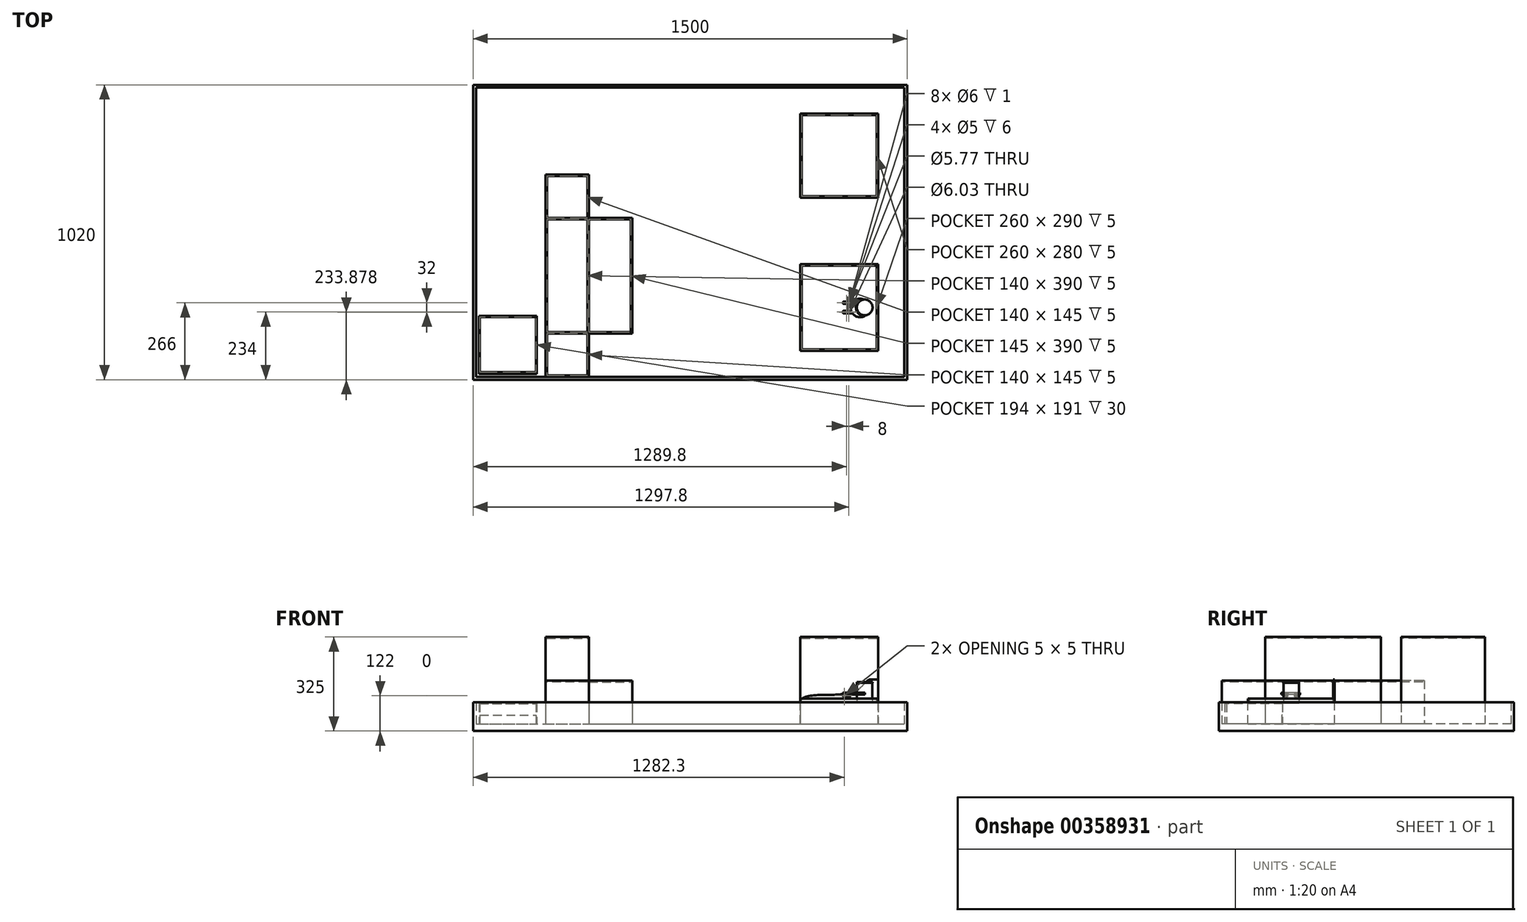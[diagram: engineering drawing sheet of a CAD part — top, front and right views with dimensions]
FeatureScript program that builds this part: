
annotation { "Feature Type Name" : "Feature", "Feature Type Description" : "" }
export const myFeature = defineFeature(function(context is Context, id is Id, definition is map)
    precondition{}
    {
        {
            var Q0;
            Q0=qCreatedBy(makeId("Top.planeOp"),FACE);
            var sketch = newSketch(context, id + "F0", { "sketchPlane" : qUnion([Q0])});
            skCircle(sketch, "E0", {"center": v(0, 0) * mm, "radius": 27.2 * mm});
            skSolve(sketch);
        }
        {
            var Q0;
            Q0=qSketchRegion(id+"F0",true);
            extrude(context, id + "F1", {"entities" : qUnion([Q0]), "depth" : 2.83 * mm});
        }
        {
            var Q0;
            Q0=makeQuery(id+"F1.opExtrude","CAP_FACE",FACE,{"disambiguationData":[OSD([sQuery(id+"F0.wireOp",EDGE,"E0")])],"isStart":false});
            var sketch = newSketch(context, id + "F2", { "sketchPlane" : qUnion([Q0])});
            skCircle(sketch, "E1", {"center": v(0, 0) * mm, "radius": 26.4 * mm});
            skSolve(sketch);
        }
        {
            var Q0;
            Q0=qSketchRegion(id+"F2",true);
            extrude(context, id + "F3", {"entities" : qUnion([Q0]), "operationType" : NewBodyOperationType.ADD, "depth" : 67.36 * mm});
        }
        {
            var Q0;
            Q0=makeQuery(id+"F3.opExtrude","CAP_FACE",FACE,{"disambiguationData":[OSD([sQuery(id+"F2.wireOp",EDGE,"E1")])],"isStart":false});
            var sketch = newSketch(context, id + "F4", { "sketchPlane" : qUnion([Q0])});
            skCircle(sketch, "E2", {"center": v(0, 0) * mm, "radius": 27.2 * mm});
            skSolve(sketch);
        }
        {
            var Q0;
            Q0=qSketchRegion(id+"F4",true);
            extrude(context, id + "F5", {"entities" : qUnion([Q0]), "operationType" : NewBodyOperationType.ADD, "depth" : 2.83 * mm});
        }
        {
            var Q0;
            Q0=makeQuery(id+"F5.opExtrude","CAP_FACE",FACE,{"disambiguationData":[OSD([sQuery(id+"F4.wireOp",EDGE,"E2")])],"isStart":false});
            var sketch = newSketch(context, id + "F6", { "sketchPlane" : qUnion([Q0])});
            skSolve(sketch);
        }
        {
            var Q0;
            Q0=qCreatedBy(makeId("Top.planeOp"),FACE);
            cPlane(context, id + "F7", {"entities" : qUnion([Q0]), "cplaneType" : CPlaneType.OFFSET, "offset" : 25 * mm, "width" : 150 * mm, "height" : 150 * mm});
        }
        {
            var Q0;
            Q0=makeQuery(id+"F6.imprint","IMPRINT",FACE,{"disambiguationData":[TD([[makeQuery(id+"F6.imprint","IMPRINT",EDGE,{"derivedFrom":makeQuery(id+"F5.opExtrude","CAP_EDGE",EDGE,{"disambiguationData":[OSD([sQuery(id+"F4.wireOp",EDGE,"E2")])],"isStart":false})}),1.0]])]});
            var sketch = newSketch(context, id + "F8", { "sketchPlane" : qUnion([Q0])});
            skSolve(sketch);
        }
        {
            var Q0;
            Q0=qCreatedBy(makeId("Top.planeOp"),FACE);
            var sketch = newSketch(context, id + "F9", { "sketchPlane" : qUnion([Q0])});
            skLineSegment(sketch, "E3.bottom", {"start": v(-222.8, -150) * mm, "end": v(47.2, -150) * mm});
            skLineSegment(sketch, "E3.top", {"start": v(-222.8, 150) * mm, "end": v(47.2, 150) * mm});
            skLineSegment(sketch, "E3.left", {"start": v(-222.8, -150) * mm, "end": v(-222.8, 150) * mm});
            skLineSegment(sketch, "E3.right", {"start": v(47.2, -150) * mm, "end": v(47.2, 150) * mm});
            skSolve(sketch);
        }
        {
            var Q0;
            Q0=qSketchRegion(id+"F9",true);
            extrude(context, id + "F10", {"entities" : qUnion([Q0]), "oppositeDirection" : true, "depth" : 72 * mm});
        }
        {
            var Q0;
            Q0=makeQuery(id+"F10.opExtrude","CAP_FACE",FACE,{"disambiguationData":[OSD([sQuery(id+"F9.wireOp",EDGE,"E3.bottom"),sQuery(id+"F9.wireOp",EDGE,"E3.top"),sQuery(id+"F9.wireOp",EDGE,"E3.left"),sQuery(id+"F9.wireOp",EDGE,"E3.right")])],"isStart":true});
            var sketch = newSketch(context, id + "F11", { "sketchPlane" : qUnion([Q0])});
            skLineSegment(sketch, "E4.bottom", {"start": v(-222.8, -150) * mm, "end": v(47.2, -150) * mm});
            skLineSegment(sketch, "E4.top", {"start": v(-222.8, -145) * mm, "end": v(42.2, -145) * mm});
            skLineSegment(sketch, "E4.left", {"start": v(-222.8, -150) * mm, "end": v(-222.8, -145) * mm});
            skLineSegment(sketch, "E5.bottom", {"start": v(47.2, 150) * mm, "end": v(42.2, 150) * mm});
            skLineSegment(sketch, "E5.left", {"start": v(47.2, 150) * mm, "end": v(47.2, -150) * mm});
            skLineSegment(sketch, "E5.right", {"start": v(42.2, 150) * mm, "end": v(42.2, -145) * mm});
            skSolve(sketch);
        }
        {
            var Q0;
            Q0=qSketchRegion(id+"F11",true);
            extrude(context, id + "F12", {"entities" : qUnion([Q0]), "operationType" : NewBodyOperationType.ADD, "depth" : 15 * mm});
        }
        {
            var Q0;
            Q0=makeQuery(id+"F12.boolean.opBoolean","MERGE",FACE,{"derivedFrom":[makeQuery(id+"F10.opExtrude","SWEPT_FACE",FACE,{"disambiguationData":[OSD([sQuery(id+"F9.wireOp",EDGE,"E3.top")])]}),makeQuery(id+"F12.opExtrude","SWEPT_FACE",FACE,{"disambiguationData":[OSD([sQuery(id+"F11.wireOp",EDGE,"E5.bottom")])]})]});
            var sketch = newSketch(context, id + "F13", { "sketchPlane" : qUnion([Q0])});
            skLineSegment(sketch, "E6", {"start": v(-47.2, 81.36) * mm, "end": v(-21.31, 81.36) * mm});
            skFitSpline(sketch, "E7", {"points": [v(-21.31, 81.36) * mm, v(15.24, 52.01) * mm, v(114.14, 28.17) * mm, v(222.8, 0) * mm], "startDerivative": vector(181.02, 0.3) * mm, "endDerivative": vector(-1.73, -239.85) * mm});
            skLineSegment(sketch, "E8", {"start": v(-47.2, 81.36) * mm, "end": v(-47.2, -72) * mm});
            skLineSegment(sketch, "E9", {"start": v(-47.2, -72) * mm, "end": v(222.8, -72) * mm});
            skLineSegment(sketch, "E10", {"start": v(222.8, -72) * mm, "end": v(222.8, 0) * mm});
            skSolve(sketch);
        }
        {
            var Q0;
            Q0=qSketchRegion(id+"F13",true);
            extrude(context, id + "F14", {"entities" : qUnion([Q0]), "operationType" : NewBodyOperationType.ADD, "oppositeDirection" : true, "depth" : 5 * mm});
        }
        {
            var Q0;
            Q0=makeQuery(id+"F10.opExtrude","CAP_FACE",FACE,{"disambiguationData":[OSD([sQuery(id+"F9.wireOp",EDGE,"E3.bottom"),sQuery(id+"F9.wireOp",EDGE,"E3.top"),sQuery(id+"F9.wireOp",EDGE,"E3.left"),sQuery(id+"F9.wireOp",EDGE,"E3.right")])],"isStart":true});
            var sketch = newSketch(context, id + "F15", { "sketchPlane" : qUnion([Q0])});
            skLineSegment(sketch, "E11.bottom", {"start": v(-222.8, 145) * mm, "end": v(-217.8, 145) * mm});
            skLineSegment(sketch, "E11.top", {"start": v(-222.8, -145) * mm, "end": v(-217.8, -145) * mm});
            skLineSegment(sketch, "E11.left", {"start": v(-222.8, 145) * mm, "end": v(-222.8, -145) * mm});
            skLineSegment(sketch, "E11.right", {"start": v(-217.8, 145) * mm, "end": v(-217.8, -145) * mm});
            skSolve(sketch);
        }
        {
            var Q0;
            Q0=qSketchRegion(id+"F15",true);
            extrude(context, id + "F16", {"entities" : qUnion([Q0]), "operationType" : NewBodyOperationType.ADD, "depth" : 5 * mm});
        }
        {
            var Q0;
            Q0=makeQuery(id+"F10.opExtrude","CAP_FACE",FACE,{"disambiguationData":[OSD([sQuery(id+"F9.wireOp",EDGE,"E3.bottom"),sQuery(id+"F9.wireOp",EDGE,"E3.top"),sQuery(id+"F9.wireOp",EDGE,"E3.left"),sQuery(id+"F9.wireOp",EDGE,"E3.right")])],"isStart":false});
            var sketch = newSketch(context, id + "F17", { "sketchPlane" : qUnion([Q0])});
            skLineSegment(sketch, "E12.bottom", {"start": v(147.2, 250) * mm, "end": v(-1352.8, 250) * mm});
            skLineSegment(sketch, "E12.top", {"start": v(147.2, -770) * mm, "end": v(-1352.8, -770) * mm});
            skLineSegment(sketch, "E12.left", {"start": v(147.2, 250) * mm, "end": v(147.2, -770) * mm});
            skLineSegment(sketch, "E12.right", {"start": v(-1352.8, 250) * mm, "end": v(-1352.8, -770) * mm});
            skSolve(sketch);
        }
        {
            var Q0;
            Q0=qSketchRegion(id+"F17",true);
            extrude(context, id + "F18", {"entities" : qUnion([Q0]), "operationType" : NewBodyOperationType.ADD, "depth" : 25 * mm});
        }
        {
            var Q0;
            Q0=makeQuery(id+"F18.opExtrude","CAP_FACE",FACE,{"disambiguationData":[OSD([sQuery(id+"F17.wireOp",EDGE,"E12.bottom"),sQuery(id+"F17.wireOp",EDGE,"E12.top"),sQuery(id+"F17.wireOp",EDGE,"E12.left"),sQuery(id+"F17.wireOp",EDGE,"E12.right")])],"isStart":true});
            var sketch = newSketch(context, id + "F19", { "sketchPlane" : qUnion([Q0])});
            skLineSegment(sketch, "E13.bottom", {"start": v(-222.8, 670) * mm, "end": v(47.2, 670) * mm});
            skLineSegment(sketch, "E13.top", {"start": v(-222.8, 380) * mm, "end": v(47.2, 380) * mm});
            skLineSegment(sketch, "E13.left", {"start": v(-222.8, 670) * mm, "end": v(-222.8, 380) * mm});
            skLineSegment(sketch, "E13.right", {"start": v(47.2, 670) * mm, "end": v(47.2, 380) * mm});
            skSolve(sketch);
        }
        {
            var Q0;
            Q0=qSketchRegion(id+"F19",true);
            extrude(context, id + "F20", {"entities" : qUnion([Q0]), "operationType" : NewBodyOperationType.ADD, "depth" : 300 * mm});
        }
        {
            var Q0;
            Q0=makeQuery(id+"F20.opExtrude","CAP_FACE",FACE,{"disambiguationData":[OSD([sQuery(id+"F19.wireOp",EDGE,"E13.bottom"),sQuery(id+"F19.wireOp",EDGE,"E13.top"),sQuery(id+"F19.wireOp",EDGE,"E13.left"),sQuery(id+"F19.wireOp",EDGE,"E13.right")])],"isStart":false});
            var sketch = newSketch(context, id + "F21", { "sketchPlane" : qUnion([Q0])});
            skLineSegment(sketch, "E14.bottom", {"start": v(-217.8, 665) * mm, "end": v(42.2, 665) * mm});
            skLineSegment(sketch, "E14.top", {"start": v(-217.8, 385) * mm, "end": v(42.2, 385) * mm});
            skLineSegment(sketch, "E14.left", {"start": v(-217.8, 665) * mm, "end": v(-217.8, 385) * mm});
            skLineSegment(sketch, "E14.right", {"start": v(42.2, 665) * mm, "end": v(42.2, 385) * mm});
            skSolve(sketch);
        }
        {
            var Q0;
            Q0=qSketchRegion(id+"F21",true);
            extrude(context, id + "F22", {"entities" : qUnion([Q0]), "operationType" : NewBodyOperationType.REMOVE, "oppositeDirection" : true, "depth" : 5 * mm});
        }
        {
            var Q0;
            Q0=makeQuery(id+"F18.opExtrude","CAP_FACE",FACE,{"disambiguationData":[OSD([sQuery(id+"F17.wireOp",EDGE,"E12.bottom"),sQuery(id+"F17.wireOp",EDGE,"E12.top"),sQuery(id+"F17.wireOp",EDGE,"E12.left"),sQuery(id+"F17.wireOp",EDGE,"E12.right")])],"isStart":true});
            var sketch = newSketch(context, id + "F23", { "sketchPlane" : qUnion([Q0])});
            skLineSegment(sketch, "E15.bottom", {"start": v(-1352.8, 770) * mm, "end": v(147.2, 770) * mm});
            skLineSegment(sketch, "E15.top", {"start": v(-1352.8, -250) * mm, "end": v(147.2, -250) * mm});
            skLineSegment(sketch, "E15.left", {"start": v(-1352.8, 770) * mm, "end": v(-1352.8, -250) * mm});
            skLineSegment(sketch, "E15.right", {"start": v(147.2, 770) * mm, "end": v(147.2, -250) * mm});
            skLineSegment(sketch, "E16.bottom", {"start": v(-1342.8, 760) * mm, "end": v(137.2, 760) * mm});
            skLineSegment(sketch, "E16.top", {"start": v(-1342.8, -240) * mm, "end": v(137.2, -240) * mm});
            skLineSegment(sketch, "E16.left", {"start": v(-1342.8, 760) * mm, "end": v(-1342.8, -240) * mm});
            skLineSegment(sketch, "E16.right", {"start": v(137.2, 760) * mm, "end": v(137.2, -240) * mm});
            skSolve(sketch);
        }
        {
            var Q0;
            Q0=qSketchRegion(id+"F23",true);
            extrude(context, id + "F24", {"entities" : qUnion([Q0]), "operationType" : NewBodyOperationType.ADD, "depth" : 75 * mm});
        }
        {
            var Q0;
            Q0=makeQuery(id+"F18.opExtrude","CAP_FACE",FACE,{"disambiguationData":[OSD([sQuery(id+"F17.wireOp",EDGE,"E12.bottom"),sQuery(id+"F17.wireOp",EDGE,"E12.top"),sQuery(id+"F17.wireOp",EDGE,"E12.left"),sQuery(id+"F17.wireOp",EDGE,"E12.right")])],"isStart":true});
            var sketch = newSketch(context, id + "F25", { "sketchPlane" : qUnion([Q0])});
            skLineSegment(sketch, "E17.bottom", {"start": v(-1102.8, 460) * mm, "end": v(-952.8, 460) * mm});
            skLineSegment(sketch, "E17.top", {"start": v(-1102.8, -240) * mm, "end": v(-952.8, -240) * mm});
            skLineSegment(sketch, "E17.left", {"start": v(-1102.8, 460) * mm, "end": v(-1102.8, -240) * mm});
            skLineSegment(sketch, "E17.right", {"start": v(-952.8, 460) * mm, "end": v(-952.8, 310) * mm});
            skLineSegment(sketch, "E18.bottom", {"start": v(-952.8, 310) * mm, "end": v(-802.8, 310) * mm});
            skLineSegment(sketch, "E18.top", {"start": v(-952.8, -90) * mm, "end": v(-802.8, -90) * mm});
            skLineSegment(sketch, "E18.right", {"start": v(-802.8, 310) * mm, "end": v(-802.8, -90) * mm});
            skLineSegment(sketch, "E19.trimOffspring", {"start": v(-952.8, -90) * mm, "end": v(-952.8, -240) * mm});
            skSolve(sketch);
        }
        {
            var Q0;
            Q0=qSketchRegion(id+"F25",true);
            extrude(context, id + "F26", {"entities" : qUnion([Q0]), "operationType" : NewBodyOperationType.ADD, "depth" : 150 * mm});
        }
        {
            var Q0;
            Q0=makeQuery(id+"F26.opExtrude","CAP_FACE",FACE,{"disambiguationData":[OSD([sQuery(id+"F25.wireOp",EDGE,"E17.bottom"),sQuery(id+"F25.wireOp",EDGE,"E17.top"),sQuery(id+"F25.wireOp",EDGE,"E17.left"),sQuery(id+"F25.wireOp",EDGE,"E17.right"),sQuery(id+"F25.wireOp",EDGE,"E18.bottom"),sQuery(id+"F25.wireOp",EDGE,"E18.top"),sQuery(id+"F25.wireOp",EDGE,"E18.right"),sQuery(id+"F25.wireOp",EDGE,"E19.trimOffspring")])],"isStart":false});
            var sketch = newSketch(context, id + "F27", { "sketchPlane" : qUnion([Q0])});
            skLineSegment(sketch, "E20.bottom", {"start": v(-952.8, 310) * mm, "end": v(-1102.8, 310) * mm});
            skLineSegment(sketch, "E20.top", {"start": v(-952.8, -90) * mm, "end": v(-1102.8, -90) * mm});
            skLineSegment(sketch, "E20.left", {"start": v(-952.8, 310) * mm, "end": v(-952.8, -90) * mm});
            skLineSegment(sketch, "E20.right", {"start": v(-1102.8, 310) * mm, "end": v(-1102.8, -90) * mm});
            skSolve(sketch);
        }
        {
            var Q0;
            Q0=qSketchRegion(id+"F27",true);
            extrude(context, id + "F28", {"entities" : qUnion([Q0]), "operationType" : NewBodyOperationType.ADD, "depth" : 150 * mm});
        }
        {
            var Q0;
            Q0=makeQuery(id+"F28.opExtrude","CAP_FACE",FACE,{"disambiguationData":[OSD([sQuery(id+"F27.wireOp",EDGE,"E20.bottom"),sQuery(id+"F27.wireOp",EDGE,"E20.top"),sQuery(id+"F27.wireOp",EDGE,"E20.left"),sQuery(id+"F27.wireOp",EDGE,"E20.right")])],"isStart":false});
            var sketch = newSketch(context, id + "F29", { "sketchPlane" : qUnion([Q0])});
            skLineSegment(sketch, "E21.bottom", {"start": v(-1097.8, 305) * mm, "end": v(-957.8, 305) * mm});
            skLineSegment(sketch, "E21.top", {"start": v(-1097.8, -85) * mm, "end": v(-957.8, -85) * mm});
            skLineSegment(sketch, "E21.left", {"start": v(-1097.8, 305) * mm, "end": v(-1097.8, -85) * mm});
            skLineSegment(sketch, "E21.right", {"start": v(-957.8, 305) * mm, "end": v(-957.8, -85) * mm});
            skSolve(sketch);
        }
        {
            var Q0;
            Q0=qSketchRegion(id+"F29",true);
            extrude(context, id + "F30", {"entities" : qUnion([Q0]), "operationType" : NewBodyOperationType.REMOVE, "oppositeDirection" : true, "depth" : 5 * mm});
        }
        {
            var Q0;
            {var subQ0=sQuery(id+"F25.wireOp",EDGE,"E17.left");var subQ1=sQuery(id+"F25.wireOp",EDGE,"E18.bottom");var subQ2=sQuery(id+"F25.wireOp",EDGE,"E17.right");var subQ3=sQuery(id+"F25.wireOp",EDGE,"E17.bottom");var subQ4=makeQuery(id+"F26.opExtrude","CAP_FACE",FACE,{"disambiguationData":[OSD([subQ3,sQuery(id+"F25.wireOp",EDGE,"E17.top"),subQ0,subQ2,subQ1,sQuery(id+"F25.wireOp",EDGE,"E18.top"),sQuery(id+"F25.wireOp",EDGE,"E18.right"),sQuery(id+"F25.wireOp",EDGE,"E19.trimOffspring")])],"isStart":false});Q0=makeQuery(id+"F28.boolean.opBoolean","SPLIT",FACE,{"disambiguationData":[TD([makeQuery(id+"F26.opExtrude","SWEPT_FACE",FACE,{"disambiguationData":[OSD([subQ3])]})])],"derivedFrom":subQ4});}
            var sketch = newSketch(context, id + "F31", { "sketchPlane" : qUnion([Q0])});
            skLineSegment(sketch, "E22.bottom", {"start": v(-1097.8, 455) * mm, "end": v(-957.8, 455) * mm});
            skLineSegment(sketch, "E22.top", {"start": v(-1097.8, 310) * mm, "end": v(-957.8, 310) * mm});
            skLineSegment(sketch, "E22.left", {"start": v(-1097.8, 455) * mm, "end": v(-1097.8, 310) * mm});
            skLineSegment(sketch, "E22.right", {"start": v(-957.8, 455) * mm, "end": v(-957.8, 310) * mm});
            skLineSegment(sketch, "E23.bottom", {"start": v(-952.8, 305) * mm, "end": v(-807.8, 305) * mm});
            skLineSegment(sketch, "E23.top", {"start": v(-952.8, -85) * mm, "end": v(-807.8, -85) * mm});
            skLineSegment(sketch, "E23.left", {"start": v(-952.8, 305) * mm, "end": v(-952.8, -85) * mm});
            skLineSegment(sketch, "E23.right", {"start": v(-807.8, 305) * mm, "end": v(-807.8, -85) * mm});
            skLineSegment(sketch, "E24.bottom", {"start": v(-1097.8, -90) * mm, "end": v(-957.8, -90) * mm});
            skLineSegment(sketch, "E24.top", {"start": v(-1097.8, -235) * mm, "end": v(-957.8, -235) * mm});
            skLineSegment(sketch, "E24.left", {"start": v(-1097.8, -90) * mm, "end": v(-1097.8, -235) * mm});
            skLineSegment(sketch, "E24.right", {"start": v(-957.8, -90) * mm, "end": v(-957.8, -235) * mm});
            skSolve(sketch);
        }
        {
            var Q0;
            Q0=qSketchRegion(id+"F31",true);
            extrude(context, id + "F32", {"entities" : qUnion([Q0]), "operationType" : NewBodyOperationType.REMOVE, "oppositeDirection" : true, "depth" : 5 * mm});
        }
        {
            var Q0;
            Q0=qCreatedBy(id+"F7.planeOp",FACE);
            var sketch = newSketch(context, id + "F33", { "sketchPlane" : qUnion([Q0])});
            skLineSegment(sketch, "E25", {"start": v(0, 0) * mm, "end": v(-90, 0) * mm, "construction": true});
            skLineSegment(sketch, "E26.bottom", {"start": v(-74.5, -12) * mm, "end": v(-55, -12) * mm});
            skLineSegment(sketch, "E26.top", {"start": v(-74.5, -20) * mm, "end": v(-55, -20) * mm});
            skLineSegment(sketch, "E26.left", {"start": v(-74.5, -12) * mm, "end": v(-74.5, -13) * mm});
            skPoint(sketch, "E27.visualSharp", {"position": v(-51, -12) * mm});
            skPoint(sketch, "E28.visualSharp", {"position": v(-51, -20) * mm});
            skCircle(sketch, "E29", {"center": v(-55, -16) * mm, "radius": 3 * mm});
            skLineSegment(sketch, "E30", {"start": v(-59, -3.98) * mm, "end": v(-59, -18.08) * mm, "construction": true});
            skCircle(sketch, "E31.MirrorC", {"center": v(-63, -16) * mm, "radius": 3 * mm});
            skLineSegment(sketch, "E32.bottom", {"start": v(-74.5, -13) * mm, "end": v(-65.65, -13) * mm});
            skLineSegment(sketch, "E32.top", {"start": v(-74.5, -19) * mm, "end": v(-65.65, -19) * mm});
            skArc(sketch, "E33", {"start": v(-65.65, -13) * mm, "mid": v(-67, -16) * mm, "end": v(-65.65, -19) * mm});
            skLineSegment(sketch, "E34.trimOffspring", {"start": v(-74.5, -19) * mm, "end": v(-74.5, -20) * mm});
            skArc(sketch, "E35.trimOffspring", {"start": v(-55, -20) * mm, "mid": v(-51, -16) * mm, "end": v(-55, -12) * mm});
            skLineSegment(sketch, "E36.MirrorCS", {"start": v(-74.5, 12) * mm, "end": v(-74.5, 13) * mm});
            skLineSegment(sketch, "E37.MirrorCS", {"start": v(-74.5, 19) * mm, "end": v(-74.5, 20) * mm});
            skPoint(sketch, "E38.MirrorP", {"position": v(-51, 12) * mm});
            skLineSegment(sketch, "E39.MirrorCS", {"start": v(-74.5, 12) * mm, "end": v(-55, 12) * mm});
            skPoint(sketch, "E40.MirrorP", {"position": v(-51, 20) * mm});
            skArc(sketch, "E41.MirrorCS", {"start": v(-65.65, 13) * mm, "mid": v(-67, 16) * mm, "end": v(-65.65, 19) * mm});
            skArc(sketch, "E42.MirrorCS", {"start": v(-55, 20) * mm, "mid": v(-51, 16) * mm, "end": v(-55, 12) * mm});
            skLineSegment(sketch, "E43.MirrorCS", {"start": v(-74.5, 20) * mm, "end": v(-55, 20) * mm});
            skCircle(sketch, "E44.MirrorC", {"center": v(-55, 16) * mm, "radius": 3 * mm});
            skCircle(sketch, "E45.MirrorC", {"center": v(-63, 16) * mm, "radius": 3 * mm});
            skLineSegment(sketch, "E46.MirrorCS", {"start": v(-74.5, 19) * mm, "end": v(-65.65, 19) * mm});
            skLineSegment(sketch, "E47.MirrorCS", {"start": v(-74.5, 13) * mm, "end": v(-65.65, 13) * mm});
            skSolve(sketch);
        }
        {
            var Q0;
            Q0=qSketchRegion(id+"F33",true);
            var Q1;
            Q1=qSketchRegion(id+"F36",true);
            extrude(context, id + "F34", {"entities" : qUnion([Q0, Q1]), "endBound" : BoundingType.SYMMETRIC, "depth" : 8 * mm});
        }
        {
            var Q0;
            Q0=makeQuery(id+"F34.opExtrude","CAP_EDGE",EDGE,{"disambiguationData":[OSD([sQuery(id+"F33.wireOp",EDGE,"E34.trimOffspring")])],"isStart":false});
            var Q1;
            Q1=makeQuery(id+"F34.opExtrude","CAP_EDGE",EDGE,{"disambiguationData":[OSD([sQuery(id+"F33.wireOp",EDGE,"E26.left")])],"isStart":false});
            var Q2;
            Q2=makeQuery(id+"F34.opExtrude","CAP_EDGE",EDGE,{"disambiguationData":[OSD([sQuery(id+"F33.wireOp",EDGE,"E34.trimOffspring")])],"isStart":true});
            var Q3;
            Q3=makeQuery(id+"F34.opExtrude","CAP_EDGE",EDGE,{"disambiguationData":[OSD([sQuery(id+"F33.wireOp",EDGE,"E26.left")])],"isStart":true});
            var Q4;
            Q4=makeQuery(id+"F34.opExtrude","CAP_EDGE",EDGE,{"disambiguationData":[OSD([sQuery(id+"F33.wireOp",EDGE,"E36.MirrorCS")])],"isStart":false});
            var Q5;
            Q5=makeQuery(id+"F34.opExtrude","CAP_EDGE",EDGE,{"disambiguationData":[OSD([sQuery(id+"F33.wireOp",EDGE,"E37.MirrorCS")])],"isStart":false});
            var Q6;
            Q6=makeQuery(id+"F34.opExtrude","CAP_EDGE",EDGE,{"disambiguationData":[OSD([sQuery(id+"F33.wireOp",EDGE,"E37.MirrorCS")])],"isStart":true});
            var Q7;
            Q7=makeQuery(id+"F34.opExtrude","CAP_EDGE",EDGE,{"disambiguationData":[OSD([sQuery(id+"F33.wireOp",EDGE,"E36.MirrorCS")])],"isStart":true});
            fillet(context, id + "F35", {"entities" : qUnion([Q0, Q1, Q2, Q3, Q4, Q5, Q6, Q7]), "radius" : 4 * mm, "tangentPropagation" : true, "allowEdgeOverflow" : false});
        }
        {
            var Q0;
            Q0=makeQuery(id+"F34.opExtrude","SWEPT_FACE",FACE,{"disambiguationData":[OSD([sQuery(id+"F33.wireOp",EDGE,"E26.top")])]});
            var sketch = newSketch(context, id + "F36", { "sketchPlane" : qUnion([Q0])});
            skCircle(sketch, "E48", {"center": v(-70.5, 25) * mm, "radius": 3 * mm});
            skSolve(sketch);
        }
        {
            var Q0;
            Q0=qSketchRegion(id+"F36",true);
            var Q1;
            Q1=makeQuery(id+"F34.opExtrude","SWEPT_FACE",FACE,{"disambiguationData":[OSD([sQuery(id+"F33.wireOp",EDGE,"E26.bottom")])]});
            extrude(context, id + "F37", {"entities" : qUnion([Q0]), "operationType" : NewBodyOperationType.ADD, "endBound" : BoundingType.UP_TO_SURFACE, "oppositeDirection" : true, "endBoundEntityFace" : qUnion([Q1]), "depth" : 25 * mm});
        }
        {
            var Q0;
            Q0=makeQuery(id+"F34.opExtrude","SWEPT_FACE",FACE,{"disambiguationData":[OSD([sQuery(id+"F33.wireOp",EDGE,"E43.MirrorCS")])]});
            var sketch = newSketch(context, id + "F38", { "sketchPlane" : qUnion([Q0])});
            skCircle(sketch, "E49", {"center": v(70.5, 25) * mm, "radius": 3 * mm});
            skSolve(sketch);
        }
        {
            var Q0;
            Q0=qSketchRegion(id+"F38",true);
            var Q1;
            Q1=makeQuery(id+"F34.opExtrude","SWEPT_FACE",FACE,{"disambiguationData":[OSD([sQuery(id+"F33.wireOp",EDGE,"E39.MirrorCS")])]});
            extrude(context, id + "F39", {"entities" : qUnion([Q0]), "operationType" : NewBodyOperationType.ADD, "endBound" : BoundingType.UP_TO_SURFACE, "oppositeDirection" : true, "endBoundEntityFace" : qUnion([Q1]), "depth" : 25 * mm});
        }
        {
            var Q0;
            Q0=qCreatedBy(id+"F7.planeOp",FACE);
            var sketch = newSketch(context, id + "F40", { "sketchPlane" : qUnion([Q0])});
            skCircle(sketch, "E50", {"center": v(-55, 16) * mm, "radius": 3 * mm});
            skCircle(sketch, "E51", {"center": v(-63, 16) * mm, "radius": 2.5 * mm});
            skCircle(sketch, "E52", {"center": v(-63, 16) * mm, "radius": 3 * mm});
            skCircle(sketch, "E53", {"center": v(-55, 16) * mm, "radius": 2.5 * mm});
            skSolve(sketch);
        }
        {
            var Q0;
            Q0=qSketchRegion(id+"F40",true);
            extrude(context, id + "F41", {"entities" : qUnion([Q0]), "operationType" : NewBodyOperationType.ADD, "endBound" : BoundingType.SYMMETRIC, "depth" : 6 * mm});
        }
        {
            var Q0;
            Q0=qCreatedBy(id+"F7.planeOp",FACE);
            var sketch = newSketch(context, id + "F42", { "sketchPlane" : qUnion([Q0])});
            skCircle(sketch, "E54", {"center": v(-63, -16) * mm, "radius": 2.5 * mm});
            skCircle(sketch, "E55", {"center": v(-63, -16) * mm, "radius": 3 * mm});
            skCircle(sketch, "E56", {"center": v(-55, -16) * mm, "radius": 2.5 * mm});
            skCircle(sketch, "E57", {"center": v(-55, -16) * mm, "radius": 3 * mm});
            skSolve(sketch);
        }
        {
            var Q0;
            Q0=qSketchRegion(id+"F42",true);
            extrude(context, id + "F43", {"entities" : qUnion([Q0]), "operationType" : NewBodyOperationType.ADD, "endBound" : BoundingType.SYMMETRIC, "depth" : 6 * mm});
        }
        {
            var Q0;
            Q0=makeQuery(id+"F34.opExtrude","SWEPT_FACE",FACE,{"disambiguationData":[OSD([sQuery(id+"F33.wireOp",EDGE,"E43.MirrorCS")])]});
            var sketch = newSketch(context, id + "F44", { "sketchPlane" : qUnion([Q0])});
            skArc(sketch, "E58", {"start": v(71.5, 27.3) * mm, "mid": v(70.5, 27.5) * mm, "end": v(69.5, 27.3) * mm});
            skLineSegment(sketch, "E59.bottom", {"start": v(68.2, 26) * mm, "end": v(69.5, 26) * mm});
            skLineSegment(sketch, "E59.top", {"start": v(68.2, 24) * mm, "end": v(69.5, 24) * mm});
            skLineSegment(sketch, "E60.left", {"start": v(71.5, 27.3) * mm, "end": v(71.5, 26) * mm});
            skLineSegment(sketch, "E60.right", {"start": v(69.5, 27.3) * mm, "end": v(69.5, 26) * mm});
            skPoint(sketch, "E61.orphan", {"position": v(69.5, 27.8) * mm});
            skPoint(sketch, "E62.orphan", {"position": v(71.5, 27.8) * mm});
            skArc(sketch, "E63.trimOffspring", {"start": v(68.2, 26) * mm, "mid": v(68, 25) * mm, "end": v(68.2, 24) * mm});
            skPoint(sketch, "E59.left.start.orphan", {"position": v(67.32, 26) * mm});
            skPoint(sketch, "E64.orphan", {"position": v(67.32, 24) * mm});
            skArc(sketch, "E65.trimOffspring", {"start": v(69.5, 22.7) * mm, "mid": v(70.5, 22.5) * mm, "end": v(71.5, 22.7) * mm});
            skLineSegment(sketch, "E66.trimOffspring", {"start": v(69.5, 24) * mm, "end": v(69.5, 22.7) * mm});
            skLineSegment(sketch, "E67.trimOffspring", {"start": v(71.5, 26) * mm, "end": v(72.8, 26) * mm});
            skLineSegment(sketch, "E68.trimOffspring", {"start": v(71.5, 24) * mm, "end": v(71.5, 22.7) * mm});
            skLineSegment(sketch, "E69.trimOffspring", {"start": v(71.5, 24) * mm, "end": v(72.8, 24) * mm});
            skPoint(sketch, "E60.top.end.orphan", {"position": v(69.5, 22.2) * mm});
            skPoint(sketch, "E70.orphan", {"position": v(71.5, 22.2) * mm});
            skPoint(sketch, "E59.right.end.orphan", {"position": v(73.68, 24) * mm});
            skPoint(sketch, "E71.orphan", {"position": v(73.68, 26) * mm});
            skArc(sketch, "E72.trimOffspring", {"start": v(72.8, 24) * mm, "mid": v(73, 25) * mm, "end": v(72.8, 26) * mm});
            skSolve(sketch);
        }
        {
            var Q0;
            Q0=qSketchRegion(id+"F44",true);
            extrude(context, id + "F45", {"entities" : qUnion([Q0]), "operationType" : NewBodyOperationType.REMOVE, "endBound" : BoundingType.THROUGH_ALL, "oppositeDirection" : true, "depth" : 25 * mm});
        }
        {
            var Q0;
            Q0=makeQuery(id+"F18.opExtrude","CAP_FACE",FACE,{"disambiguationData":[OSD([sQuery(id+"F17.wireOp",EDGE,"E12.bottom"),sQuery(id+"F17.wireOp",EDGE,"E12.top"),sQuery(id+"F17.wireOp",EDGE,"E12.left"),sQuery(id+"F17.wireOp",EDGE,"E12.right")])],"isStart":true});
            var sketch = newSketch(context, id + "F46", { "sketchPlane" : qUnion([Q0])});
            skLineSegment(sketch, "E73.bottom", {"start": v(-1332.8, -30) * mm, "end": v(-1132.8, -30) * mm});
            skLineSegment(sketch, "E73.top", {"start": v(-1332.8, -230) * mm, "end": v(-1132.8, -230) * mm});
            skLineSegment(sketch, "E73.left", {"start": v(-1332.8, -30) * mm, "end": v(-1332.8, -230) * mm});
            skLineSegment(sketch, "E73.right", {"start": v(-1132.8, -30) * mm, "end": v(-1132.8, -230) * mm});
            skLineSegment(sketch, "E74.bottom", {"start": v(-1329.8, -33) * mm, "end": v(-1135.8, -33) * mm});
            skLineSegment(sketch, "E74.top", {"start": v(-1329.8, -224) * mm, "end": v(-1135.8, -224) * mm});
            skLineSegment(sketch, "E74.left", {"start": v(-1329.8, -33) * mm, "end": v(-1329.8, -224) * mm});
            skLineSegment(sketch, "E74.right", {"start": v(-1135.8, -33) * mm, "end": v(-1135.8, -224) * mm});
            skSolve(sketch);
        }
        {
            var Q0;
            Q0=qSketchRegion(id+"F46",true);
            extrude(context, id + "F47", {"entities" : qUnion([Q0]), "operationType" : NewBodyOperationType.ADD, "depth" : 30 * mm});
        }
        {
            var Q0;
            Q0=makeQuery(id+"F47.opExtrude","CAP_FACE",FACE,{"disambiguationData":[OSD([sQuery(id+"F46.wireOp",EDGE,"E73.bottom"),sQuery(id+"F46.wireOp",EDGE,"E73.top"),sQuery(id+"F46.wireOp",EDGE,"E73.left"),sQuery(id+"F46.wireOp",EDGE,"E73.right"),sQuery(id+"F46.wireOp",EDGE,"E74.bottom"),sQuery(id+"F46.wireOp",EDGE,"E74.top"),sQuery(id+"F46.wireOp",EDGE,"E74.left"),sQuery(id+"F46.wireOp",EDGE,"E74.right")])],"isStart":false});
            var sketch = newSketch(context, id + "F48", { "sketchPlane" : qUnion([Q0])});
            skLineSegment(sketch, "E75.bottom", {"start": v(-1332.8, -30) * mm, "end": v(-1329.8, -30) * mm});
            skLineSegment(sketch, "E75.top", {"start": v(-1332.8, -230) * mm, "end": v(-1329.8, -230) * mm});
            skLineSegment(sketch, "E75.left", {"start": v(-1332.8, -30) * mm, "end": v(-1332.8, -230) * mm});
            skLineSegment(sketch, "E75.right", {"start": v(-1329.8, -30) * mm, "end": v(-1329.8, -224) * mm});
            skLineSegment(sketch, "E76.bottom", {"start": v(-1329.8, -230) * mm, "end": v(-1135.8, -230) * mm});
            skLineSegment(sketch, "E76.top", {"start": v(-1329.8, -224) * mm, "end": v(-1135.8, -224) * mm});
            skLineSegment(sketch, "E77.bottom", {"start": v(-1135.8, -230) * mm, "end": v(-1132.8, -230) * mm});
            skLineSegment(sketch, "E77.top", {"start": v(-1135.8, -30) * mm, "end": v(-1132.8, -30) * mm});
            skLineSegment(sketch, "E77.left", {"start": v(-1135.8, -224) * mm, "end": v(-1135.8, -30) * mm});
            skLineSegment(sketch, "E77.right", {"start": v(-1132.8, -230) * mm, "end": v(-1132.8, -30) * mm});
            skSolve(sketch);
        }
        {
            var Q0;
            Q0=qSketchRegion(id+"F48",true);
            extrude(context, id + "F49", {"entities" : qUnion([Q0]), "operationType" : NewBodyOperationType.ADD, "depth" : 40 * mm});
        }
        {
            var Q0;
            Q0=makeQuery(id+"F34.opExtrude","CAP_FACE",FACE,{"disambiguationData":[OSD([sQuery(id+"F33.wireOp",EDGE,"E36.MirrorCS"),sQuery(id+"F33.wireOp",EDGE,"E37.MirrorCS"),sQuery(id+"F33.wireOp",EDGE,"E39.MirrorCS"),sQuery(id+"F33.wireOp",EDGE,"E41.MirrorCS"),sQuery(id+"F33.wireOp",EDGE,"E42.MirrorCS"),sQuery(id+"F33.wireOp",EDGE,"E43.MirrorCS"),sQuery(id+"F33.wireOp",EDGE,"E44.MirrorC"),sQuery(id+"F33.wireOp",EDGE,"E45.MirrorC"),sQuery(id+"F33.wireOp",EDGE,"E46.MirrorCS"),sQuery(id+"F33.wireOp",EDGE,"E47.MirrorCS")])],"isStart":false});
            var sketch = newSketch(context, id + "F50", { "sketchPlane" : qUnion([Q0])});
            skLineSegment(sketch, "E78", {"start": v(-72.27, -20.05) * mm, "end": v(-42, -20.05) * mm});
            skCircle(sketch, "E79", {"center": v(-63, 16) * mm, "radius": 2.86 * mm});
            skArc(sketch, "E80", {"start": v(-4.24, 27.83) * mm, "mid": v(-22.78, 29.2) * mm, "end": v(-38.94, 20) * mm});
            skArc(sketch, "E81", {"start": v(-4.24, 27.83) * mm, "mid": v(-30.1, -3.3) * mm, "end": v(1.09, -29.1) * mm});
            skPoint(sketch, "E82.end.orphan", {"position": v(-46.04, -11.73) * mm});
            skLineSegment(sketch, "E83", {"start": v(-72.23, -11.41) * mm, "end": v(-46.04, -11.73) * mm});
            skArc(sketch, "E84.trimOffspring", {"start": v(-42.08, -20.05) * mm, "mid": v(-22.3, -33.22) * mm, "end": v(1.09, -29.1) * mm});
            skLineSegment(sketch, "E85", {"start": v(-75.27, -14.41) * mm, "end": v(-75.27, -17.05) * mm});
            skArc(sketch, "E86.trimOffspring", {"start": v(-44.48, 12) * mm, "mid": v(-47.61, 0.3) * mm, "end": v(-46.16, -11.73) * mm});
            skLineSegment(sketch, "E87", {"start": v(-38.94, 20) * mm, "end": v(-71.84, 20) * mm});
            skLineSegment(sketch, "E88", {"start": v(-44.48, 12) * mm, "end": v(-71.84, 12) * mm});
            skLineSegment(sketch, "E89", {"start": v(-74.84, 17) * mm, "end": v(-74.84, 15) * mm});
            skCircle(sketch, "E90", {"center": v(-55, 16) * mm, "radius": 2.88 * mm});
            skCircle(sketch, "E91", {"center": v(-55, -16.12) * mm, "radius": 3.02 * mm});
            skCircle(sketch, "E92", {"center": v(-63, -16) * mm, "radius": 2.86 * mm});
            skArc(sketch, "E93.filletArc", {"start": v(-71.84, 20) * mm, "mid": v(-73.96, 19.12) * mm, "end": v(-74.84, 17) * mm});
            skArc(sketch, "E94.filletArc", {"start": v(-74.84, 15) * mm, "mid": v(-73.96, 12.88) * mm, "end": v(-71.84, 12) * mm});
            skArc(sketch, "E95.filletArc", {"start": v(-72.23, -11.41) * mm, "mid": v(-74.38, -12.28) * mm, "end": v(-75.27, -14.41) * mm});
            skArc(sketch, "E96.filletArc", {"start": v(-75.27, -17.05) * mm, "mid": v(-74.4, -19.17) * mm, "end": v(-72.27, -20.05) * mm});
            skSolve(sketch);
        }
        {
            var Q0;
            Q0 = qSketchRegion(id + "F50", true);
            extrude(context, id + "F51", {"entities" : qUnion([Q0]), "depth" : 6 * mm});
        }
    });
